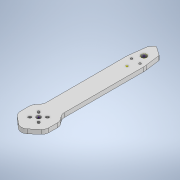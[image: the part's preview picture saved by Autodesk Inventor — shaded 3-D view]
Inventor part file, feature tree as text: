
AUTODESK INVENTOR PART (.ipt)
format: ipt  version: 2020 (Build 240168000, 168)  size: 169,984 bytes
history: native  units: mm
features: sketch x2, extrude x1
ambient origin geometry x8: Origin, YZ Plane, XZ Plane, XY Plane, X Axis, Y Axis, Z Axis, Center Point
bodies: Solid1 (feature_tree)
feature tree (3):
  extrude  "Extrusion1"  [1 undecoded]
  sketch  "Sketch2"
  sketch  "Sketch1"  dims[d0=6.0mm d1=0.0mm]
note: 1 required parameter value undecoded (feature->parameter linkage not recoverable at this tier; creation-order binding heuristic only, values carry confidence <= 0.55)
